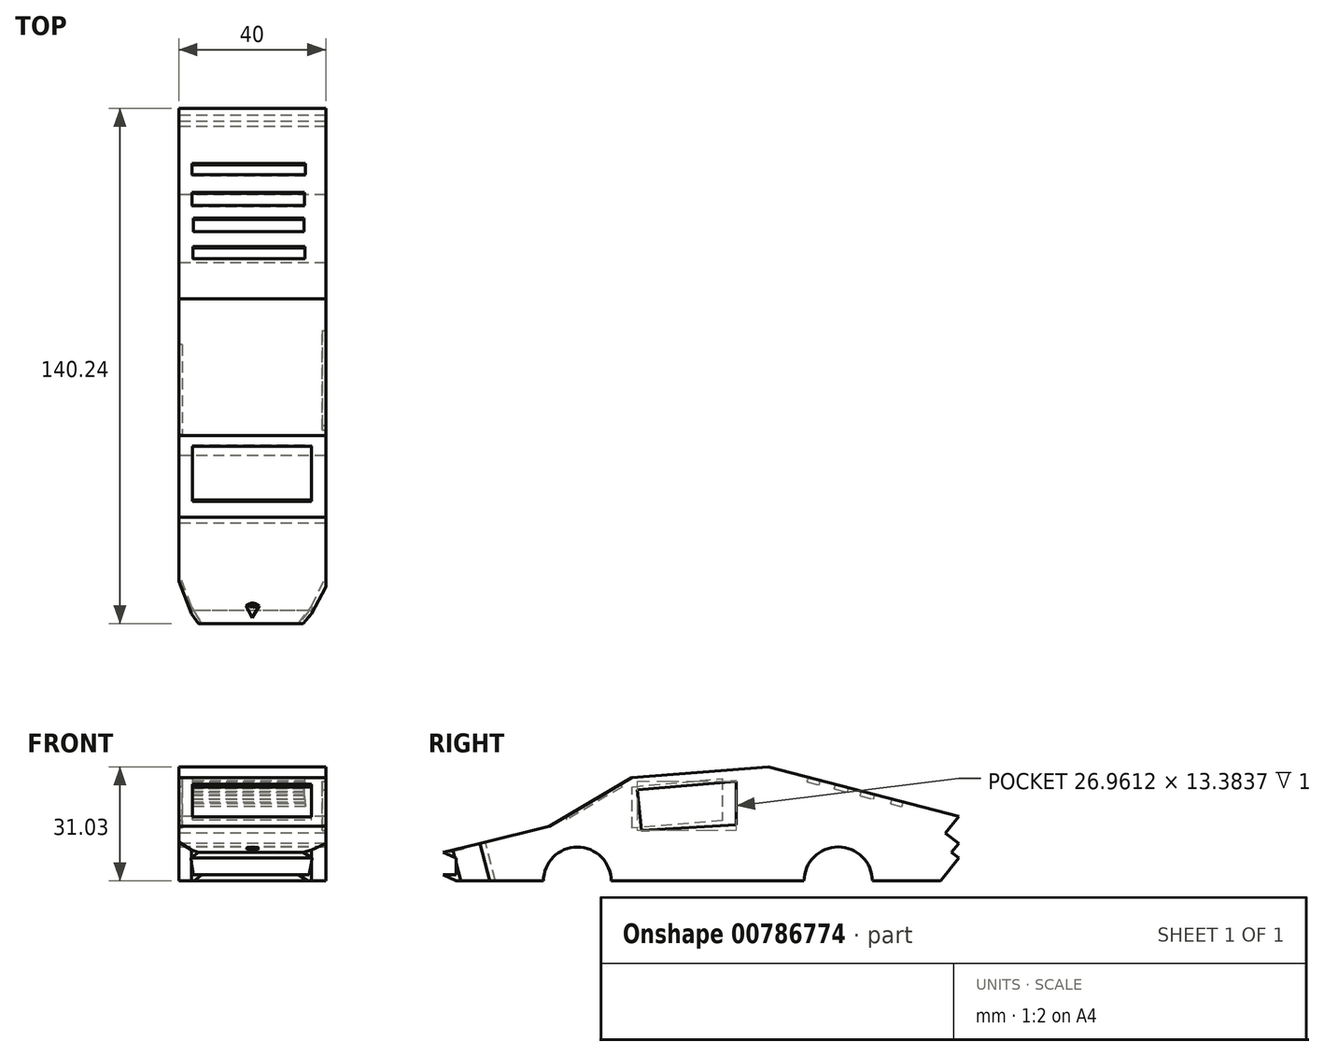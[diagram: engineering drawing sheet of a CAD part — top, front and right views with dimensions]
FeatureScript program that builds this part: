
annotation { "Feature Type Name" : "Feature", "Feature Type Description" : "" }
export const myFeature = defineFeature(function(context is Context, id is Id, definition is map)
    precondition{}
    {
        {
            var Q0;
            Q0=qCreatedBy(makeId("Right.planeOp"),FACE);
            var sketch = newSketch(context, id + "F0", { "sketchPlane" : qUnion([Q0])});
            skLineSegment(sketch, "E0", {"start": v(-41.8, 4.36) * mm, "end": v(-70.7, -2.81) * mm});
            skLineSegment(sketch, "E1", {"start": v(-70.7, -2.81) * mm, "end": v(-67.2, -4.36) * mm});
            skLineSegment(sketch, "E2", {"start": v(-67.2, -4.36) * mm, "end": v(-67.2, -8.83) * mm});
            skLineSegment(sketch, "E3", {"start": v(-67.2, -8.83) * mm, "end": v(-70.7, -8.83) * mm});
            skLineSegment(sketch, "E4", {"start": v(-70.7, -8.83) * mm, "end": v(-67.2, -10.57) * mm});
            skLineSegment(sketch, "E5", {"start": v(-67.2, -10.57) * mm, "end": v(64.57, -10.57) * mm});
            skLineSegment(sketch, "E6", {"start": v(64.57, -10.57) * mm, "end": v(69.54, -4.36) * mm});
            skLineSegment(sketch, "E7", {"start": v(69.54, -4.36) * mm, "end": v(67.6, -2.81) * mm});
            skLineSegment(sketch, "E8", {"start": v(67.6, -2.81) * mm, "end": v(69.54, -0.39) * mm});
            skLineSegment(sketch, "E9", {"start": v(69.54, -0.39) * mm, "end": v(65.94, 2.49) * mm});
            skLineSegment(sketch, "E10", {"start": v(65.94, 2.49) * mm, "end": v(69.54, 6.98) * mm});
            skLineSegment(sketch, "E11", {"start": v(69.54, 6.98) * mm, "end": v(17.75, 20.46) * mm});
            skLineSegment(sketch, "E12", {"start": v(17.75, 20.46) * mm, "end": v(-19.5, 17.55) * mm});
            skLineSegment(sketch, "E13", {"start": v(-19.5, 17.55) * mm, "end": v(-41.8, 4.36) * mm});
            skCircle(sketch, "E14", {"center": v(-34.23, -10.57) * mm, "radius": 9.21 * mm});
            skCircle(sketch, "E15", {"center": v(36.76, -10.57) * mm, "radius": 9.29 * mm});
            skSolve(sketch);
        }
        {
            var Q0;
            Q0=makeQuery(id+"F0.imprint","IMPRINT",FACE,{"disambiguationData":[TD([[makeQuery(id+"F0.imprint","IMPRINT",EDGE,{"derivedFrom":sQuery(id+"F0.wireOp",EDGE,"E0")}),1.0]])]});
            extrude(context, id + "F1", {"entities" : qUnion([Q0]), "endBound" : BoundingType.SYMMETRIC, "depth" : 40 * mm, "offsetDistance" : 25 * mm});
        }
        {
            var Q0;
            Q0=makeQuery(id+"F1.opExtrude","CAP_FACE",FACE,{"disambiguationData":[OSD([sQuery(id+"F0.wireOp",EDGE,"E0"),sQuery(id+"F0.wireOp",EDGE,"E1"),sQuery(id+"F0.wireOp",EDGE,"E2"),sQuery(id+"F0.wireOp",EDGE,"E3"),sQuery(id+"F0.wireOp",EDGE,"E4"),sQuery(id+"F0.wireOp",EDGE,"E5"),sQuery(id+"F0.wireOp",EDGE,"E6"),sQuery(id+"F0.wireOp",EDGE,"E7"),sQuery(id+"F0.wireOp",EDGE,"E8"),sQuery(id+"F0.wireOp",EDGE,"E9"),sQuery(id+"F0.wireOp",EDGE,"E10"),sQuery(id+"F0.wireOp",EDGE,"E11"),sQuery(id+"F0.wireOp",EDGE,"E12"),sQuery(id+"F0.wireOp",EDGE,"E13"),sQuery(id+"F0.wireOp",EDGE,"E14"),sQuery(id+"F0.wireOp",EDGE,"E15")])],"isStart":true});
            cPlane(context, id + "F2", {"entities" : qUnion([Q0]), "cplaneType" : CPlaneType.OFFSET, "offset" : 25 * mm, "width" : 150 * mm, "height" : 150 * mm});
        }
        {
            var Q0;
            Q0=qCreatedBy(id+"F2.planeOp",FACE);
            var sketch = newSketch(context, id + "F3", { "sketchPlane" : qUnion([Q0])});
            skLineSegment(sketch, "E16", {"start": v(-5.24, 17.3) * mm, "end": v(19.3, 15.05) * mm});
            skLineSegment(sketch, "E17", {"start": v(19.3, 15.05) * mm, "end": v(19.3, 3.82) * mm});
            skLineSegment(sketch, "E18", {"start": v(19.3, 3.82) * mm, "end": v(-5.24, 5.9) * mm});
            skLineSegment(sketch, "E19", {"start": v(-5.24, 5.9) * mm, "end": v(-5.24, 17.3) * mm});
            skSolve(sketch);
        }
        {
            var Q0;
            Q0=makeQuery(id+"F3.imprint","IMPRINT",FACE,{"disambiguationData":[TD([[makeQuery(id+"F3.imprint","IMPRINT",EDGE,{"derivedFrom":sQuery(id+"F3.wireOp",EDGE,"E16")}),-1.0]])]});
            extrude(context, id + "F4", {"entities" : qUnion([Q0]), "operationType" : NewBodyOperationType.REMOVE, "oppositeDirection" : true, "depth" : 26 * mm, "offsetDistance" : 25 * mm});
        }
        {
            var Q0;
            Q0=makeQuery(id+"F1.opExtrude","CAP_FACE",FACE,{"disambiguationData":[OSD([sQuery(id+"F0.wireOp",EDGE,"E0"),sQuery(id+"F0.wireOp",EDGE,"E1"),sQuery(id+"F0.wireOp",EDGE,"E2"),sQuery(id+"F0.wireOp",EDGE,"E3"),sQuery(id+"F0.wireOp",EDGE,"E4"),sQuery(id+"F0.wireOp",EDGE,"E5"),sQuery(id+"F0.wireOp",EDGE,"E6"),sQuery(id+"F0.wireOp",EDGE,"E7"),sQuery(id+"F0.wireOp",EDGE,"E8"),sQuery(id+"F0.wireOp",EDGE,"E9"),sQuery(id+"F0.wireOp",EDGE,"E10"),sQuery(id+"F0.wireOp",EDGE,"E11"),sQuery(id+"F0.wireOp",EDGE,"E12"),sQuery(id+"F0.wireOp",EDGE,"E13"),sQuery(id+"F0.wireOp",EDGE,"E14"),sQuery(id+"F0.wireOp",EDGE,"E15")])],"isStart":false});
            cPlane(context, id + "F5", {"entities" : qUnion([Q0]), "cplaneType" : CPlaneType.OFFSET, "offset" : 25 * mm, "width" : 150 * mm, "height" : 150 * mm});
        }
        {
            var Q0;
            Q0=qCreatedBy(id+"F5.planeOp",FACE);
            var sketch = newSketch(context, id + "F6", { "sketchPlane" : qUnion([Q0])});
            skLineSegment(sketch, "E20", {"start": v(-17.94, 14.26) * mm, "end": v(9.02, 16.58) * mm});
            skLineSegment(sketch, "E21", {"start": v(9.02, 16.58) * mm, "end": v(9.02, 4.75) * mm});
            skLineSegment(sketch, "E22", {"start": v(9.02, 4.75) * mm, "end": v(-16.78, 3.2) * mm});
            skLineSegment(sketch, "E23", {"start": v(-16.78, 3.2) * mm, "end": v(-17.94, 14.26) * mm});
            skSolve(sketch);
        }
        {
            var Q0;
            Q0=makeQuery(id+"F6.imprint","IMPRINT",FACE,{"disambiguationData":[TD([[makeQuery(id+"F6.imprint","IMPRINT",EDGE,{"derivedFrom":sQuery(id+"F6.wireOp",EDGE,"E20")}),-1.0]])]});
            extrude(context, id + "F7", {"entities" : qUnion([Q0]), "operationType" : NewBodyOperationType.REMOVE, "oppositeDirection" : true, "depth" : 26 * mm, "offsetDistance" : 25 * mm});
        }
        {
            var Q0;
            Q0=makeQuery(id+"F1.opExtrude","SWEPT_FACE",FACE,{"disambiguationData":[OSD([sQuery(id+"F0.wireOp",EDGE,"E13")])]});
            cPlane(context, id + "F8", {"entities" : qUnion([Q0]), "cplaneType" : CPlaneType.OFFSET, "offset" : 25 * mm, "width" : 150 * mm, "height" : 150 * mm});
        }
        {
            var Q0;
            Q0=qCreatedBy(id+"F8.planeOp",FACE);
            var sketch = newSketch(context, id + "F9", { "sketchPlane" : qUnion([Q0])});
            skLineSegment(sketch, "E24.bottom", {"start": v(-16.23, -11.33) * mm, "end": v(16.1, -11.33) * mm});
            skLineSegment(sketch, "E24.top", {"start": v(-16.23, -28.73) * mm, "end": v(16.1, -28.73) * mm});
            skLineSegment(sketch, "E24.left", {"start": v(-16.23, -11.33) * mm, "end": v(-16.23, -28.73) * mm});
            skLineSegment(sketch, "E24.right", {"start": v(16.1, -11.33) * mm, "end": v(16.1, -28.73) * mm});
            skSolve(sketch);
        }
        {
            var Q0;
            Q0=makeQuery(id+"F9.imprint","IMPRINT",FACE,{"disambiguationData":[TD([[makeQuery(id+"F9.imprint","IMPRINT",EDGE,{"derivedFrom":sQuery(id+"F9.wireOp",EDGE,"E24.bottom")}),-1.0]])]});
            extrude(context, id + "F10", {"entities" : qUnion([Q0]), "operationType" : NewBodyOperationType.REMOVE, "oppositeDirection" : true, "depth" : 25.9 * mm, "offsetDistance" : 25 * mm});
        }
        {
            var Q0;
            Q0=makeQuery(id+"F1.opExtrude","SWEPT_FACE",FACE,{"disambiguationData":[OSD([sQuery(id+"F0.wireOp",EDGE,"E11")])]});
            cPlane(context, id + "F11", {"entities" : qUnion([Q0]), "cplaneType" : CPlaneType.OFFSET, "offset" : 25 * mm, "width" : 150 * mm, "height" : 150 * mm});
        }
        {
            var Q0;
            Q0=qCreatedBy(id+"F11.planeOp",FACE);
            var sketch = newSketch(context, id + "F12", { "sketchPlane" : qUnion([Q0])});
            skLineSegment(sketch, "E25.bottom", {"start": v(14.31, 23.28) * mm, "end": v(-16.1, 23.28) * mm});
            skLineSegment(sketch, "E25.top", {"start": v(14.31, 26.64) * mm, "end": v(-16.1, 26.64) * mm});
            skLineSegment(sketch, "E25.left", {"start": v(14.31, 23.28) * mm, "end": v(14.31, 26.64) * mm});
            skLineSegment(sketch, "E25.right", {"start": v(-16.1, 23.28) * mm, "end": v(-16.1, 26.64) * mm});
            skLineSegment(sketch, "E26.bottom", {"start": v(14.08, 30.9) * mm, "end": v(-15.97, 30.9) * mm});
            skLineSegment(sketch, "E26.top", {"start": v(14.08, 34.6) * mm, "end": v(-15.97, 34.6) * mm});
            skLineSegment(sketch, "E26.left", {"start": v(14.08, 30.9) * mm, "end": v(14.08, 34.6) * mm});
            skLineSegment(sketch, "E26.right", {"start": v(-15.97, 30.9) * mm, "end": v(-15.97, 34.6) * mm});
            skLineSegment(sketch, "E27.bottom", {"start": v(14.18, 38.2) * mm, "end": v(-16.33, 38.2) * mm});
            skLineSegment(sketch, "E27.top", {"start": v(14.18, 41.9) * mm, "end": v(-16.33, 41.9) * mm});
            skLineSegment(sketch, "E27.left", {"start": v(14.18, 38.2) * mm, "end": v(14.18, 41.9) * mm});
            skLineSegment(sketch, "E27.right", {"start": v(-16.33, 38.2) * mm, "end": v(-16.33, 41.9) * mm});
            skLineSegment(sketch, "E28.bottom", {"start": v(14.5, 46.8) * mm, "end": v(-16.33, 46.8) * mm});
            skLineSegment(sketch, "E28.top", {"start": v(14.5, 49.96) * mm, "end": v(-16.33, 49.96) * mm});
            skLineSegment(sketch, "E28.left", {"start": v(14.5, 46.8) * mm, "end": v(14.5, 49.96) * mm});
            skLineSegment(sketch, "E28.right", {"start": v(-16.33, 46.8) * mm, "end": v(-16.33, 49.96) * mm});
            skSolve(sketch);
        }
        {
            var Q0;
            Q0=makeQuery(id+"F12.imprint","IMPRINT",FACE,{"disambiguationData":[TD([[makeQuery(id+"F12.imprint","IMPRINT",EDGE,{"derivedFrom":sQuery(id+"F12.wireOp",EDGE,"E26.bottom")}),-1.0]])]});
            var Q1;
            Q1=makeQuery(id+"F12.imprint","IMPRINT",FACE,{"disambiguationData":[TD([[makeQuery(id+"F12.imprint","IMPRINT",EDGE,{"derivedFrom":sQuery(id+"F12.wireOp",EDGE,"E27.bottom")}),-1.0]])]});
            var Q2;
            Q2=makeQuery(id+"F12.imprint","IMPRINT",FACE,{"disambiguationData":[TD([[makeQuery(id+"F12.imprint","IMPRINT",EDGE,{"derivedFrom":sQuery(id+"F12.wireOp",EDGE,"E28.bottom")}),-1.0]])]});
            var Q3;
            Q3=makeQuery(id+"F12.imprint","IMPRINT",FACE,{"disambiguationData":[TD([[makeQuery(id+"F12.imprint","IMPRINT",EDGE,{"derivedFrom":sQuery(id+"F12.wireOp",EDGE,"E25.bottom")}),-1.0]])]});
            extrude(context, id + "F13", {"entities" : qUnion([Q0, Q1, Q2, Q3]), "operationType" : NewBodyOperationType.REMOVE, "oppositeDirection" : true, "depth" : 26.3 * mm, "offsetDistance" : 25 * mm});
        }
        {
            var Q0;
            Q0=makeQuery(id+"F1.opExtrude","SWEPT_FACE",FACE,{"disambiguationData":[OSD([sQuery(id+"F0.wireOp",EDGE,"E0")])]});
            cPlane(context, id + "F14", {"entities" : qUnion([Q0]), "cplaneType" : CPlaneType.OFFSET, "offset" : 25 * mm, "width" : 150 * mm, "height" : 150 * mm});
        }
        {
            var Q0;
            Q0=qCreatedBy(id+"F14.planeOp",FACE);
            var sketch = newSketch(context, id + "F15", { "sketchPlane" : qUnion([Q0])});
            skArc(sketch, "E29", {"start": v(1.94, -64.36) * mm, "mid": v(0.16, -63.56) * mm, "end": v(-1.65, -64.32) * mm});
            skLineSegment(sketch, "E30", {"start": v(-1.65, -64.32) * mm, "end": v(0, -67.72) * mm});
            skLineSegment(sketch, "E31", {"start": v(0, -67.72) * mm, "end": v(1.94, -64.36) * mm});
            skText(sketch, "E32", { "text": "lamborghini", "fontName": "OpenSans-Regular.ttf"});
            const initialGuessF15  = {"E32": [-0.00139, -0.06458, 1, 0, 0.00036]};
            skSetInitialGuess(sketch, initialGuessF15);
            skSolve(sketch);
        }
        {
            var Q0;
            Q0 = qSketchRegion(id + "F15", true);
            extrude(context, id + "F16", {"entities" : qUnion([Q0]), "operationType" : NewBodyOperationType.REMOVE, "oppositeDirection" : true, "depth" : 25.3 * mm, "offsetDistance" : 25 * mm});
        }
        {
            var Q0;
            Q0=qCreatedBy(id+"F14.planeOp",FACE);
            var sketch = newSketch(context, id + "F17", { "sketchPlane" : qUnion([Q0])});
            skLineSegment(sketch, "E33", {"start": v(9.39, -74.48) * mm, "end": v(16.1, -66.6) * mm});
            skLineSegment(sketch, "E34", {"start": v(16.1, -66.6) * mm, "end": v(21.34, -56.35) * mm});
            skLineSegment(sketch, "E35", {"start": v(21.34, -56.35) * mm, "end": v(23.32, -75.07) * mm});
            skLineSegment(sketch, "E36", {"start": v(23.32, -75.07) * mm, "end": v(9.39, -74.48) * mm});
            skLineSegment(sketch, "E37", {"start": v(-11.07, -74.48) * mm, "end": v(-16.55, -66.6) * mm});
            skLineSegment(sketch, "E38", {"start": v(-16.55, -66.6) * mm, "end": v(-20.42, -56.35) * mm});
            skLineSegment(sketch, "E39", {"start": v(-20.42, -56.35) * mm, "end": v(-26.52, -74.48) * mm});
            skLineSegment(sketch, "E40", {"start": v(-26.52, -74.48) * mm, "end": v(-11.07, -74.48) * mm});
            skSolve(sketch);
        }
        {
            var Q0;
            Q0=makeQuery(id+"F17.imprint","IMPRINT",FACE,{"disambiguationData":[TD([[makeQuery(id+"F17.imprint","IMPRINT",EDGE,{"derivedFrom":sQuery(id+"F17.wireOp",EDGE,"E37")}),1.0]])]});
            var Q1;
            Q1=makeQuery(id+"F17.imprint","IMPRINT",FACE,{"disambiguationData":[TD([[makeQuery(id+"F17.imprint","IMPRINT",EDGE,{"derivedFrom":sQuery(id+"F17.wireOp",EDGE,"E33")}),-1.0]])]});
            extrude(context, id + "F18", {"entities" : qUnion([Q0, Q1]), "operationType" : NewBodyOperationType.REMOVE, "oppositeDirection" : true, "depth" : 44.4 * mm, "offsetDistance" : 25 * mm});
        }
    });
